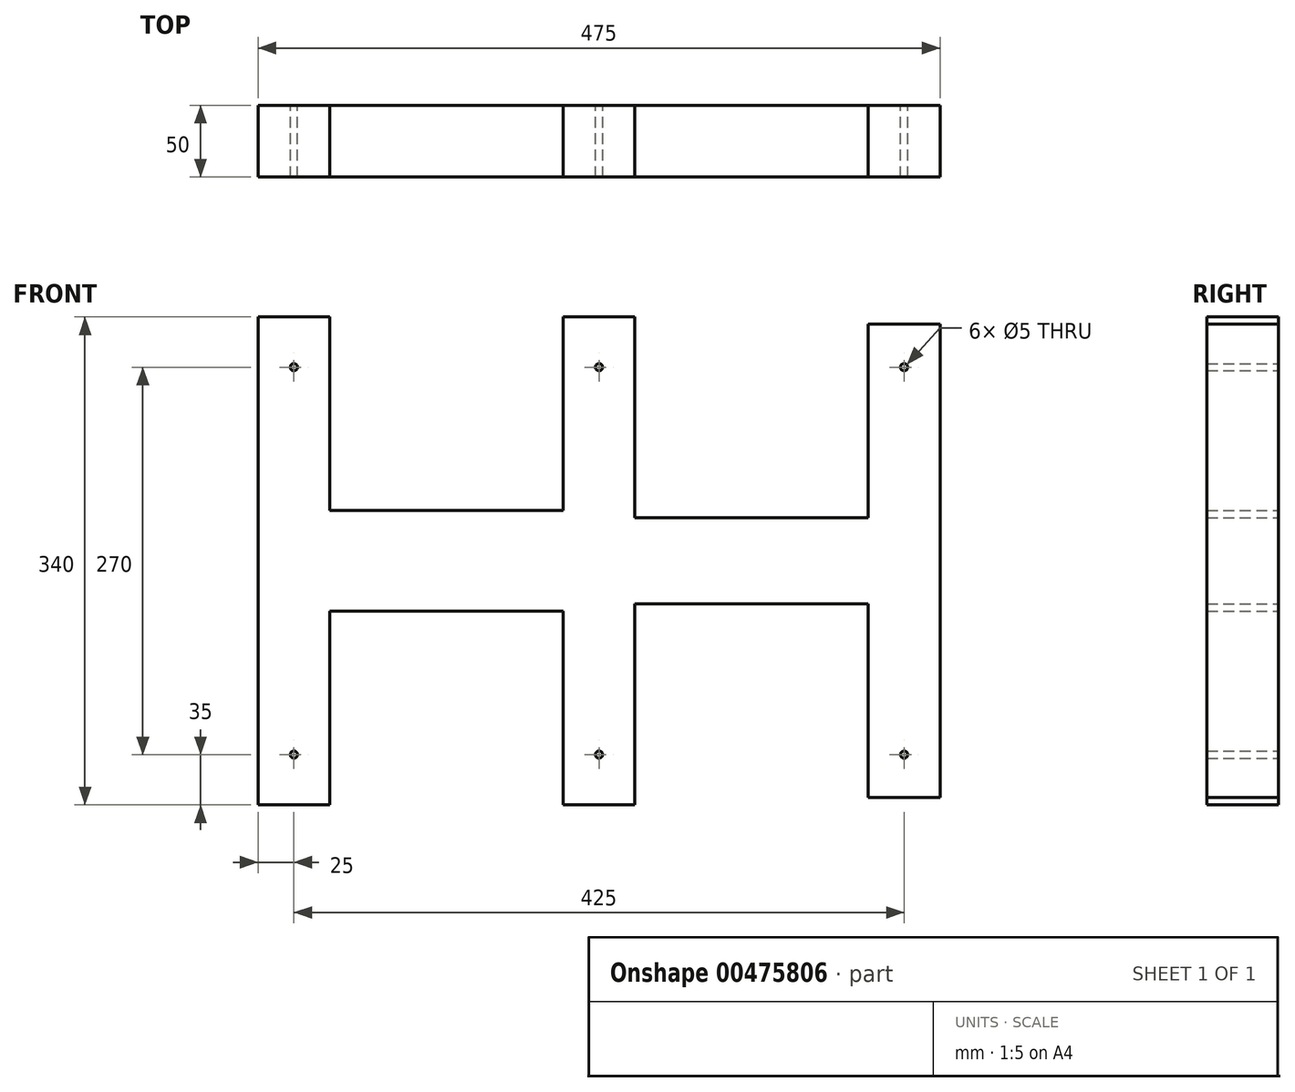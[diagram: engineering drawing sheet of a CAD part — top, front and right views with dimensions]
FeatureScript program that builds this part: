
annotation { "Feature Type Name" : "Feature", "Feature Type Description" : "" }
export const myFeature = defineFeature(function(context is Context, id is Id, definition is map)
    precondition{}
    {
        {
            var Q0;
            Q0=qCreatedBy(makeId("Front.planeOp"),FACE);
            var sketch = newSketch(context, id + "F0", { "sketchPlane" : qUnion([Q0])});
            skLineSegment(sketch, "E0", {"start": v(0, 0) * mm, "end": v(0, 170) * mm});
            skLineSegment(sketch, "E1", {"start": v(0, 170) * mm, "end": v(50, 170) * mm});
            skLineSegment(sketch, "E2", {"start": v(50, 170) * mm, "end": v(50, 35) * mm});
            skLineSegment(sketch, "E3", {"start": v(50, -35) * mm, "end": v(212.5, -35) * mm});
            skLineSegment(sketch, "E4", {"start": v(212.5, 35) * mm, "end": v(212.5, 170) * mm});
            skLineSegment(sketch, "E5", {"start": v(212.5, 170) * mm, "end": v(262.5, 170) * mm});
            skLineSegment(sketch, "E6", {"start": v(262.5, 170) * mm, "end": v(262.5, 30) * mm});
            skLineSegment(sketch, "E7", {"start": v(262.5, -30) * mm, "end": v(425, -30) * mm});
            skLineSegment(sketch, "E8", {"start": v(425, 30) * mm, "end": v(425, 165) * mm});
            skLineSegment(sketch, "E9", {"start": v(425, 165) * mm, "end": v(475, 165) * mm});
            skLineSegment(sketch, "E10", {"start": v(475, 165) * mm, "end": v(475, 0) * mm});
            skLineSegment(sketch, "E11", {"start": v(0, 0) * mm, "end": v(475, 0) * mm, "construction": true});
            skLineSegment(sketch, "E12.MirrorCS", {"start": v(0, 0) * mm, "end": v(0, -170) * mm});
            skLineSegment(sketch, "E13.MirrorCS", {"start": v(50, -170) * mm, "end": v(50, -35) * mm});
            skLineSegment(sketch, "E14.MirrorCS", {"start": v(50, 35) * mm, "end": v(212.5, 35) * mm});
            skLineSegment(sketch, "E15.MirrorCS", {"start": v(212.5, -35) * mm, "end": v(212.5, -170) * mm});
            skLineSegment(sketch, "E16.MirrorCS", {"start": v(212.5, -170) * mm, "end": v(262.5, -170) * mm});
            skLineSegment(sketch, "E17.MirrorCS", {"start": v(262.5, -170) * mm, "end": v(262.5, -30) * mm});
            skLineSegment(sketch, "E18.MirrorCS", {"start": v(262.5, 30) * mm, "end": v(425, 30) * mm});
            skLineSegment(sketch, "E19.MirrorCS", {"start": v(425, -165) * mm, "end": v(475, -165) * mm});
            skLineSegment(sketch, "E20.MirrorCS", {"start": v(0, -170) * mm, "end": v(50, -170) * mm});
            skLineSegment(sketch, "E21.MirrorCS", {"start": v(475, -165) * mm, "end": v(475, 0) * mm});
            skCircle(sketch, "E22", {"center": v(25, 135) * mm, "radius": 2.5 * mm});
            skPoint(sketch, "E22.centerSnap0", {"position": v(25, 170) * mm});
            skCircle(sketch, "E23.MirrorC", {"center": v(25, -135) * mm, "radius": 2.5 * mm});
            skLineSegment(sketch, "E24", {"start": v(237.5, -170) * mm, "end": v(237.5, 170) * mm, "construction": true});
            skCircle(sketch, "E25.MirrorC", {"center": v(450, -135) * mm, "radius": 2.5 * mm});
            skCircle(sketch, "E26.MirrorC", {"center": v(450, 135) * mm, "radius": 2.5 * mm});
            skPoint(sketch, "E27.orphan", {"position": v(50, 35) * mm});
            skPoint(sketch, "E28.orphan", {"position": v(262.5, 30) * mm});
            skLineSegment(sketch, "E29.trimOffspring", {"start": v(425, -30) * mm, "end": v(425, -165) * mm});
            skCircle(sketch, "E30", {"center": v(237.5, -135) * mm, "radius": 2.5 * mm});
            skCircle(sketch, "E31.MirrorC", {"center": v(237.5, 135) * mm, "radius": 2.5 * mm});
            skSolve(sketch);
        }
        {
            var Q0;
            Q0=makeQuery(id+"F0.imprint","IMPRINT",FACE,{"disambiguationData":[TD([[makeQuery(id+"F0.imprint","IMPRINT",EDGE,{"derivedFrom":sQuery(id+"F0.wireOp",EDGE,"E0")}),-1.0]])]});
            extrude(context, id + "F1", {"entities" : qUnion([Q0]), "depth" : 50 * mm, "offsetDistance" : 25 * mm});
        }
    });
